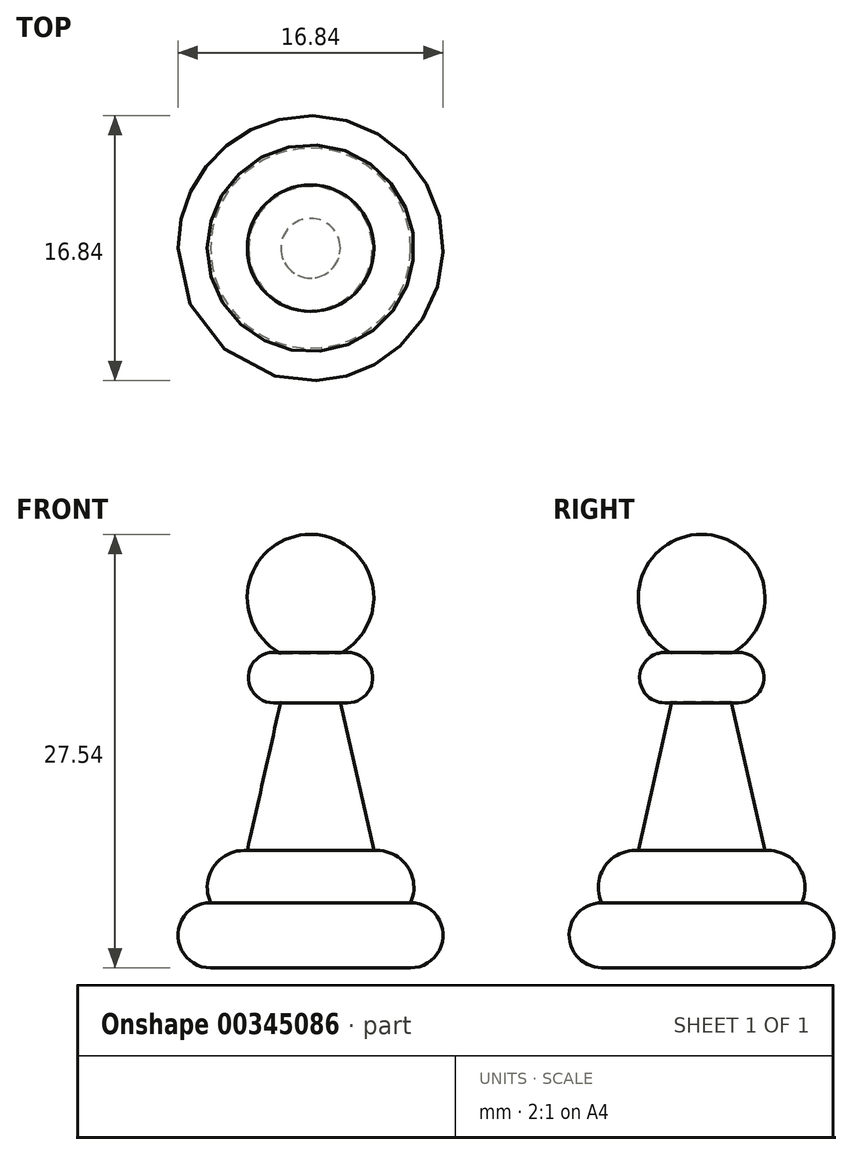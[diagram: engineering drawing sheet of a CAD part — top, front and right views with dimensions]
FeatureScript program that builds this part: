
annotation { "Feature Type Name" : "Feature", "Feature Type Description" : "" }
export const myFeature = defineFeature(function(context is Context, id is Id, definition is map)
    precondition{}
    {
        {
            var Q0;
            Q0=qCreatedBy(makeId("Front.planeOp"),FACE);
            var sketch = newSketch(context, id + "F0", { "sketchPlane" : qUnion([Q0])});
            skLineSegment(sketch, "E0", {"start": v(0, 0) * mm, "end": v(6.35, 0) * mm});
            skArc(sketch, "E1", {"start": v(6.35, 0) * mm, "mid": v(8.42, 2.07) * mm, "end": v(6.35, 4.14) * mm});
            skArc(sketch, "E2", {"start": v(6.35, 4.14) * mm, "mid": v(6.14, 6.46) * mm, "end": v(4.02, 7.45) * mm});
            skLineSegment(sketch, "E3", {"start": v(4.02, 7.45) * mm, "end": v(1.9, 16.9) * mm});
            skArc(sketch, "E4", {"start": v(1.9, 16.9) * mm, "mid": v(3.95, 18.44) * mm, "end": v(1.9, 19.97) * mm});
            skArc(sketch, "E5", {"start": v(1.9, 19.97) * mm, "mid": v(3.9, 24.5) * mm, "end": v(0, 27.54) * mm});
            skLineSegment(sketch, "E6", {"start": v(0, 0) * mm, "end": v(0, 27.54) * mm});
            skSolve(sketch);
        }
        {
            var Q0;
            Q0 = qSketchRegion(id + "F0", true);
            var Q1;
            Q1=sQuery(id+"F0.wireOp",EDGE,"E6");
            revolve(context, id + "F1", {"entities" : qUnion([Q0]), "axis" : qUnion([Q1]), "revolveType" : RevolveType.FULL});
        }
    });
